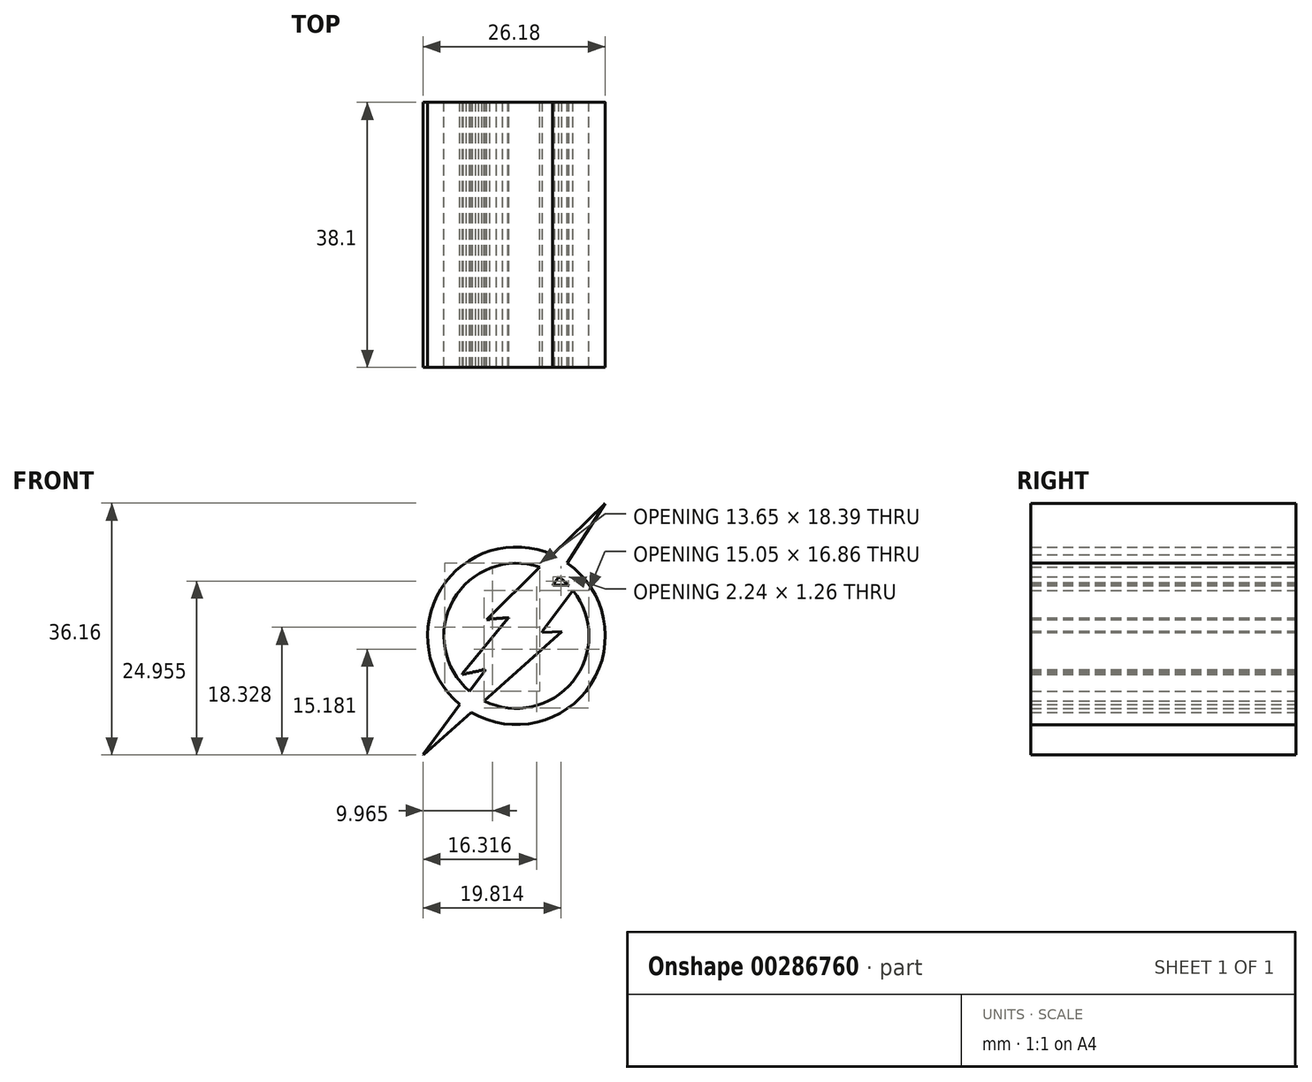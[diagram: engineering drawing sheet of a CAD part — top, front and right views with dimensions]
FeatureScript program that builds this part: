
annotation { "Feature Type Name" : "Feature", "Feature Type Description" : "" }
export const myFeature = defineFeature(function(context is Context, id is Id, definition is map)
    precondition{}
    {
        {
            var Q0;
            Q0=qCreatedBy(makeId("Front.planeOp"),FACE);
            var sketch = newSketch(context, id + "F0", { "sketchPlane" : qUnion([Q0])});
            skLineSegment(sketch, "E0", {"start": v(32.33, 37.52) * mm, "end": v(15.32, 20.8) * mm});
            skLineSegment(sketch, "E1", {"start": v(15.32, 20.8) * mm, "end": v(15.8, 20.8) * mm});
            skLineSegment(sketch, "E2", {"start": v(15.8, 20.8) * mm, "end": v(15.8, 20.9) * mm});
            skLineSegment(sketch, "E3", {"start": v(15.8, 20.9) * mm, "end": v(16.76, 20.9) * mm});
            skLineSegment(sketch, "E4", {"start": v(16.76, 20.9) * mm, "end": v(16.76, 20.98) * mm});
            skLineSegment(sketch, "E5", {"start": v(16.76, 20.98) * mm, "end": v(17.63, 20.98) * mm});
            skLineSegment(sketch, "E6", {"start": v(17.63, 20.98) * mm, "end": v(17.63, 21.06) * mm});
            skLineSegment(sketch, "E7", {"start": v(17.63, 21.06) * mm, "end": v(18.5, 21.06) * mm});
            skLineSegment(sketch, "E8", {"start": v(18.5, 21.06) * mm, "end": v(18.5, 20.98) * mm});
            skLineSegment(sketch, "E9", {"start": v(18.5, 20.98) * mm, "end": v(18.38, 20.98) * mm});
            skLineSegment(sketch, "E10", {"start": v(18.38, 20.98) * mm, "end": v(11.84, 13.01) * mm});
            skLineSegment(sketch, "E11", {"start": v(11.84, 13.01) * mm, "end": v(11.84, 12.9) * mm});
            skLineSegment(sketch, "E12", {"start": v(11.84, 12.9) * mm, "end": v(12, 12.9) * mm});
            skLineSegment(sketch, "E13", {"start": v(12, 12.9) * mm, "end": v(12, 12.98) * mm});
            skLineSegment(sketch, "E14", {"start": v(12, 12.98) * mm, "end": v(12.43, 12.98) * mm});
            skLineSegment(sketch, "E15", {"start": v(12.43, 12.98) * mm, "end": v(12.43, 13.08) * mm});
            skLineSegment(sketch, "E16", {"start": v(12.43, 13.08) * mm, "end": v(12.85, 13.08) * mm});
            skLineSegment(sketch, "E17", {"start": v(12.85, 13.08) * mm, "end": v(12.85, 13.17) * mm});
            skLineSegment(sketch, "E18", {"start": v(12.85, 13.17) * mm, "end": v(13.3, 13.17) * mm});
            skLineSegment(sketch, "E19", {"start": v(13.3, 13.17) * mm, "end": v(13.3, 13.29) * mm});
            skLineSegment(sketch, "E20", {"start": v(13.3, 13.29) * mm, "end": v(13.76, 13.29) * mm});
            skLineSegment(sketch, "E21", {"start": v(13.76, 13.29) * mm, "end": v(13.76, 13.37) * mm});
            skLineSegment(sketch, "E22", {"start": v(13.76, 13.37) * mm, "end": v(14.19, 13.37) * mm});
            skLineSegment(sketch, "E23", {"start": v(14.19, 13.37) * mm, "end": v(14.19, 13.46) * mm});
            skLineSegment(sketch, "E24", {"start": v(14.19, 13.46) * mm, "end": v(14.64, 13.46) * mm});
            skLineSegment(sketch, "E25", {"start": v(14.64, 13.46) * mm, "end": v(14.64, 13.58) * mm});
            skLineSegment(sketch, "E26", {"start": v(14.64, 13.58) * mm, "end": v(15.09, 13.58) * mm});
            skLineSegment(sketch, "E27", {"start": v(15.09, 13.58) * mm, "end": v(15.09, 13.37) * mm});
            skLineSegment(sketch, "E28", {"start": v(15.09, 13.37) * mm, "end": v(15, 13.37) * mm});
            skLineSegment(sketch, "E29", {"start": v(15, 13.37) * mm, "end": v(6.18, 1.44) * mm});
            skLineSegment(sketch, "E30", {"start": v(6.18, 1.44) * mm, "end": v(6.28, 1.36) * mm});
            skLineSegment(sketch, "E31", {"start": v(6.28, 1.36) * mm, "end": v(26.1, 19.04) * mm});
            skLineSegment(sketch, "E32", {"start": v(26.1, 19.04) * mm, "end": v(23.33, 18.93) * mm});
            skLineSegment(sketch, "E33", {"start": v(23.33, 18.93) * mm, "end": v(23.32, 19.13) * mm});
            skLineSegment(sketch, "E34", {"start": v(23.32, 19.13) * mm, "end": v(28.19, 25.57) * mm});
            skLineSegment(sketch, "E35", {"start": v(28.19, 25.57) * mm, "end": v(28.19, 25.68) * mm});
            skLineSegment(sketch, "E36", {"start": v(28.19, 25.68) * mm, "end": v(27, 25.68) * mm});
            skLineSegment(sketch, "E37", {"start": v(27, 25.68) * mm, "end": v(27, 25.75) * mm});
            skLineSegment(sketch, "E38", {"start": v(27, 25.75) * mm, "end": v(24.88, 25.75) * mm});
            skLineSegment(sketch, "E39", {"start": v(24.88, 25.75) * mm, "end": v(24.88, 25.78) * mm});
            skLineSegment(sketch, "E40", {"start": v(24.88, 25.78) * mm, "end": v(24.93, 25.78) * mm});
            skLineSegment(sketch, "E41", {"start": v(24.93, 25.78) * mm, "end": v(24.93, 25.97) * mm});
            skLineSegment(sketch, "E42", {"start": v(24.93, 25.97) * mm, "end": v(25.03, 25.96) * mm});
            skLineSegment(sketch, "E43", {"start": v(25.03, 25.96) * mm, "end": v(25.03, 26.12) * mm});
            skLineSegment(sketch, "E44", {"start": v(25.03, 26.12) * mm, "end": v(25.13, 26.12) * mm});
            skLineSegment(sketch, "E45", {"start": v(25.13, 26.12) * mm, "end": v(32.33, 37.52) * mm});
            skSolve(sketch);
        }
        {
            var Q0;
            Q0=qCreatedBy(makeId("Front.planeOp"),FACE);
            var sketch = newSketch(context, id + "F1", { "sketchPlane" : qUnion([Q0])});
            skCircle(sketch, "E46", {"center": v(19.6, 18.46) * mm, "radius": 12.76 * mm});
            skCircle(sketch, "E47", {"center": v(19.6, 18.46) * mm, "radius": 10.43 * mm});
            skSolve(sketch);
        }
        {
            var Q0;
            Q0=qSketchRegion(id+"F0",true);
            extrude(context, id + "F2", {"entities" : qUnion([Q0]), "depth" : 38.1 * mm});
        }
        {
            var Q0;
            Q0=makeQuery(id+"F1.imprint","IMPRINT",FACE,{"disambiguationData":[TD([[makeQuery(id+"F1.imprint","IMPRINT",EDGE,{"derivedFrom":sQuery(id+"F1.wireOp",EDGE,"E46")}),1.0]])]});
            extrude(context, id + "F3", {"entities" : qUnion([Q0]), "operationType" : NewBodyOperationType.ADD, "depth" : 38.1 * mm});
        }
    });
